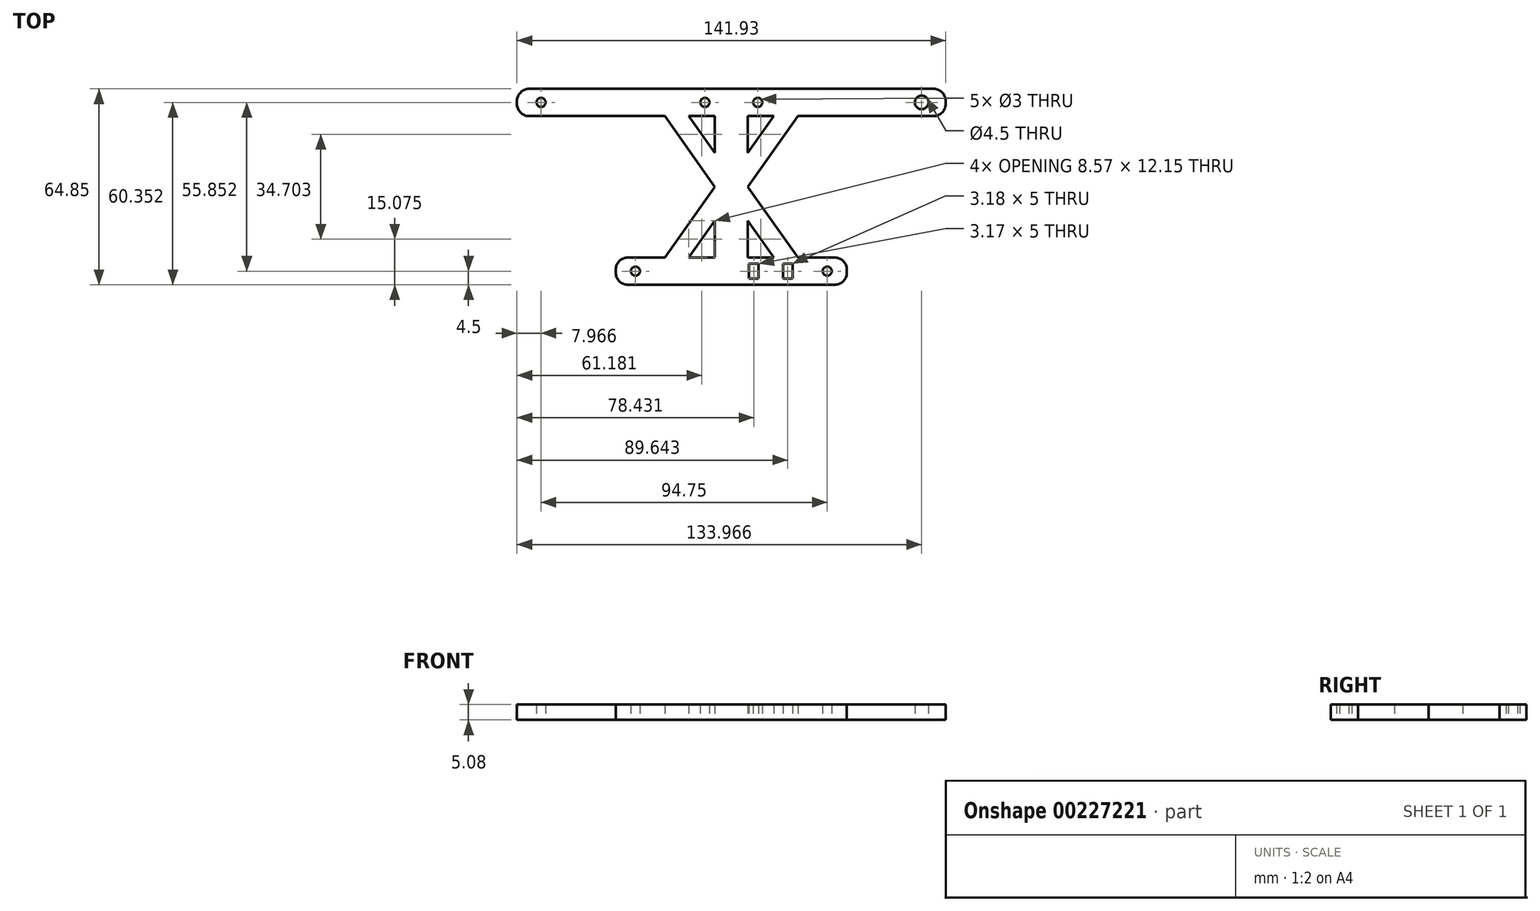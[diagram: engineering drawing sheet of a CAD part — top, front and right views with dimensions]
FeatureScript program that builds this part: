
annotation { "Feature Type Name" : "Feature", "Feature Type Description" : "" }
export const myFeature = defineFeature(function(context is Context, id is Id, definition is map)
    precondition{}
    {
        {
            var Q0;
            Q0=qCreatedBy(makeId("Top.planeOp"),FACE);
            var sketch = newSketch(context, id + "F0", { "sketchPlane" : qUnion([Q0])});
            skCircle(sketch, "E0", {"center": v(-52.08, 55.85) * mm, "radius": 1.5 * mm});
            skCircle(sketch, "E1", {"center": v(-20.83, 0) * mm, "radius": 1.5 * mm});
            skLineSegment(sketch, "E2", {"start": v(-20.83, 0) * mm, "end": v(10.92, 0) * mm});
            skLineSegment(sketch, "E3", {"start": v(-20.83, 0) * mm, "end": v(-52.08, 55.85) * mm});
            skLineSegment(sketch, "E4", {"start": v(-52.08, 55.85) * mm, "end": v(10.92, 55.85) * mm});
            skPoint(sketch, "E5.middle", {"position": v(10.92, 55.85) * mm});
            skPoint(sketch, "E6.middle", {"position": v(10.92, 0) * mm});
            skLineSegment(sketch, "E7", {"start": v(10.92, 0) * mm, "end": v(10.92, 55.85) * mm});
            skPoint(sketch, "E8.middle", {"position": v(10.92, 27.93) * mm});
            skLineSegment(sketch, "E9.MirrorCS", {"start": v(73.92, 55.85) * mm, "end": v(10.92, 55.85) * mm});
            skLineSegment(sketch, "E10.MirrorCS", {"start": v(42.67, 0) * mm, "end": v(73.92, 55.85) * mm});
            skLineSegment(sketch, "E11.MirrorCS", {"start": v(42.67, 0) * mm, "end": v(10.92, 0) * mm});
            skCircle(sketch, "E12.MirrorC", {"center": v(42.67, 0) * mm, "radius": 1.5 * mm});
            skPoint(sketch, "E13.middle", {"position": v(73.92, 55.85) * mm});
            skCircle(sketch, "E14", {"center": v(73.92, 55.85) * mm, "radius": 2.25 * mm});
            skLineSegment(sketch, "E15.bottom", {"start": v(81.88, 60.35) * mm, "end": v(-60.05, 60.35) * mm});
            skLineSegment(sketch, "E15.top", {"start": v(81.88, 51.35) * mm, "end": v(-60.05, 51.35) * mm});
            skLineSegment(sketch, "E15.left", {"start": v(81.88, 60.35) * mm, "end": v(81.88, 51.35) * mm});
            skLineSegment(sketch, "E15.right", {"start": v(-60.05, 60.35) * mm, "end": v(-60.05, 51.35) * mm});
            skLineSegment(sketch, "E16.bottom", {"start": v(49.17, 4.5) * mm, "end": v(-27.34, 4.5) * mm});
            skLineSegment(sketch, "E16.top", {"start": v(49.17, -4.5) * mm, "end": v(-27.34, -4.5) * mm});
            skLineSegment(sketch, "E16.left", {"start": v(49.17, 4.5) * mm, "end": v(49.17, -4.5) * mm});
            skLineSegment(sketch, "E16.right", {"start": v(-27.34, 4.5) * mm, "end": v(-27.34, -4.5) * mm});
            skLineSegment(sketch, "E17", {"start": v(5.42, 51.35) * mm, "end": v(5.42, 4.5) * mm});
            skLineSegment(sketch, "E18.MirrorCS", {"start": v(16.42, 51.35) * mm, "end": v(16.42, 4.5) * mm});
            skLineSegment(sketch, "E19", {"start": v(5.42, 27.93) * mm, "end": v(16.42, 27.93) * mm});
            skLineSegment(sketch, "E20", {"start": v(-11.1, 51.35) * mm, "end": v(5.42, 27.93) * mm});
            skLineSegment(sketch, "E21", {"start": v(-3.15, 51.35) * mm, "end": v(5.42, 39.2) * mm});
            skLineSegment(sketch, "E22.MirrorCS", {"start": v(24.99, 51.35) * mm, "end": v(16.42, 39.2) * mm});
            skLineSegment(sketch, "E23.MirrorCS", {"start": v(32.94, 51.35) * mm, "end": v(16.42, 27.93) * mm});
            skLineSegment(sketch, "E24.MirrorCS", {"start": v(32.94, 4.5) * mm, "end": v(16.42, 27.93) * mm});
            skLineSegment(sketch, "E25.MirrorCS", {"start": v(24.99, 4.5) * mm, "end": v(16.42, 16.65) * mm});
            skLineSegment(sketch, "E26.MirrorCS", {"start": v(-3.15, 4.5) * mm, "end": v(5.42, 16.65) * mm});
            skLineSegment(sketch, "E27.MirrorCS", {"start": v(-11.1, 4.5) * mm, "end": v(5.42, 27.93) * mm});
            skLineSegment(sketch, "E28.bottom", {"start": v(31.18, 2.5) * mm, "end": v(28, 2.5) * mm});
            skLineSegment(sketch, "E28.top", {"start": v(31.18, -2.5) * mm, "end": v(28, -2.5) * mm});
            skLineSegment(sketch, "E28.left", {"start": v(31.18, 2.5) * mm, "end": v(31.18, -2.5) * mm});
            skLineSegment(sketch, "E28.right", {"start": v(28, 2.5) * mm, "end": v(28, -2.5) * mm});
            skPoint(sketch, "E28.middle", {"position": v(29.6, 0) * mm});
            skCircle(sketch, "E29", {"center": v(19.67, 55.85) * mm, "radius": 1.5 * mm});
            skCircle(sketch, "E30.MirrorC", {"center": v(2.17, 55.85) * mm, "radius": 1.5 * mm});
            skLineSegment(sketch, "E31.bottom", {"start": v(19.97, 2.5) * mm, "end": v(16.8, 2.5) * mm});
            skLineSegment(sketch, "E31.top", {"start": v(19.97, -2.5) * mm, "end": v(16.8, -2.5) * mm});
            skLineSegment(sketch, "E31.left", {"start": v(19.97, 2.5) * mm, "end": v(19.97, -2.5) * mm});
            skLineSegment(sketch, "E31.right", {"start": v(16.8, 2.5) * mm, "end": v(16.8, -2.5) * mm});
            skSolve(sketch);
        }
        {
            var Q0;
            {var subQ5=sQuery(id+"F0.wireOp",EDGE,"E0");var subQ7=sQuery(id+"F0.wireOp",EDGE,"E3");var subQ8=makeQuery(id+"F0.imprint","INTERSECT",VERTEX,{"derivedFrom":[subQ5,subQ7]});Q0=makeQuery(id+"F0.imprint","IMPRINT",FACE,{"disambiguationData":[TD([[makeQuery(id+"F0.imprint","IMPRINT",EDGE,{"disambiguationData":[TD([[subQ8,-1.0]])],"derivedFrom":subQ5}),-1.0]])]});}
            var Q1;
            {var subQ1=sQuery(id+"F0.wireOp",EDGE,"E2");var subQ5=sQuery(id+"F0.wireOp",EDGE,"E1");var subQ6=makeQuery(id+"F0.imprint","INTERSECT",VERTEX,{"derivedFrom":[subQ5,subQ1]});Q1=makeQuery(id+"F0.imprint","IMPRINT",FACE,{"disambiguationData":[TD([[makeQuery(id+"F0.imprint","IMPRINT",EDGE,{"disambiguationData":[TD([[subQ6,-1.0]])],"derivedFrom":subQ5}),-1.0]])]});}
            var Q2;
            Q2=makeQuery(id+"F0.imprint","IMPRINT",FACE,{"disambiguationData":[TD([[makeQuery(id+"F0.imprint","IMPRINT",EDGE,{"derivedFrom":sQuery(id+"F0.wireOp",EDGE,"E15.bottom")}),1.0]])]});
            var Q3;
            Q3=makeQuery(id+"F0.imprint","IMPRINT",FACE,{"disambiguationData":[TD([[makeQuery(id+"F0.imprint","IMPRINT",EDGE,{"derivedFrom":sQuery(id+"F0.wireOp",EDGE,"E16.top")}),-1.0]])]});
            var Q4;
            {var subQ1=sQuery(id+"F0.wireOp",EDGE,"E10.MirrorCS");var subQ5=sQuery(id+"F0.wireOp",EDGE,"E16.bottom");var subQ6=makeQuery(id+"F0.imprint","INTERSECT",VERTEX,{"derivedFrom":[subQ1,subQ5]});Q4=makeQuery(id+"F0.imprint","IMPRINT",FACE,{"disambiguationData":[TD([[makeQuery(id+"F0.imprint","IMPRINT",EDGE,{"disambiguationData":[TD([[subQ6,1.0]])],"derivedFrom":subQ1}),1.0]])]});}
            var Q5;
            {var subQ0=sQuery(id+"F0.wireOp",EDGE,"E15.top");var subQ1=sQuery(id+"F0.wireOp",EDGE,"E10.MirrorCS");var subQ2=makeQuery(id+"F0.imprint","INTERSECT",VERTEX,{"derivedFrom":[subQ1,subQ0]});Q5=makeQuery(id+"F0.imprint","IMPRINT",FACE,{"disambiguationData":[TD([[makeQuery(id+"F0.imprint","IMPRINT",EDGE,{"disambiguationData":[TD([[subQ2,-1.0]])],"derivedFrom":subQ1}),1.0]])]});}
            var Q6;
            {var subQ5=sQuery(id+"F0.wireOp",EDGE,"E17");Q6=makeQuery(id+"F0.imprint","IMPRINT",FACE,{"disambiguationData":[TD([[makeQuery(id+"F0.imprint","IMPRINT",EDGE,{"derivedFrom":subQ5}),1.0]])]});}
            var Q7;
            {var subQ5=sQuery(id+"F0.wireOp",EDGE,"E18.MirrorCS");Q7=makeQuery(id+"F0.imprint","IMPRINT",FACE,{"disambiguationData":[TD([[makeQuery(id+"F0.imprint","IMPRINT",EDGE,{"derivedFrom":subQ5}),-1.0]])]});}
            var Q8;
            {var subQ0=sQuery(id+"F0.wireOp",EDGE,"feb966cf-f615-44a7-a13d-1bd144c4b3750.MirrorCS");Q8=makeQuery(id+"F0.imprint","IMPRINT",FACE,{"disambiguationData":[TD([[makeQuery(id+"F0.imprint","IMPRINT",EDGE,{"derivedFrom":subQ0}),-1.0]])]});}
            var Q9;
            {var subQ0=sQuery(id+"F0.wireOp",EDGE,"d3fe900e-5d7e-4329-a638-1e34b492a3660.MirrorCS");Q9=makeQuery(id+"F0.imprint","IMPRINT",FACE,{"disambiguationData":[TD([[makeQuery(id+"F0.imprint","IMPRINT",EDGE,{"derivedFrom":subQ0}),1.0]])]});}
            var Q10;
            {var subQ0=sQuery(id+"F0.wireOp",EDGE,"hfX9tZ72-0kb9-5i1I-bADh-dzFUvOyJdu75");Q10=makeQuery(id+"F0.imprint","IMPRINT",FACE,{"disambiguationData":[TD([[makeQuery(id+"F0.imprint","IMPRINT",EDGE,{"derivedFrom":subQ0}),-1.0]])]});}
            var Q11;
            {var subQ0=sQuery(id+"F0.wireOp",EDGE,"7ac03fb2-961d-4cd1-b936-0828aa2fb5720.MirrorCS");Q11=makeQuery(id+"F0.imprint","IMPRINT",FACE,{"disambiguationData":[TD([[makeQuery(id+"F0.imprint","IMPRINT",EDGE,{"derivedFrom":subQ0}),-1.0]])]});}
            var Q12;
            {var subQ0=sQuery(id+"F0.wireOp",EDGE,"E20");Q12=makeQuery(id+"F0.imprint","IMPRINT",FACE,{"disambiguationData":[TD([[makeQuery(id+"F0.imprint","IMPRINT",EDGE,{"derivedFrom":subQ0}),1.0]])]});}
            var Q13;
            {var subQ0=sQuery(id+"F0.wireOp",EDGE,"E26.MirrorCS");Q13=makeQuery(id+"F0.imprint","IMPRINT",FACE,{"disambiguationData":[TD([[makeQuery(id+"F0.imprint","IMPRINT",EDGE,{"derivedFrom":subQ0}),1.0]])]});}
            var Q14;
            {var subQ0=sQuery(id+"F0.wireOp",EDGE,"E24.MirrorCS");Q14=makeQuery(id+"F0.imprint","IMPRINT",FACE,{"disambiguationData":[TD([[makeQuery(id+"F0.imprint","IMPRINT",EDGE,{"derivedFrom":subQ0}),1.0]])]});}
            var Q15;
            {var subQ0=sQuery(id+"F0.wireOp",EDGE,"E22.MirrorCS");Q15=makeQuery(id+"F0.imprint","IMPRINT",FACE,{"disambiguationData":[TD([[makeQuery(id+"F0.imprint","IMPRINT",EDGE,{"derivedFrom":subQ0}),1.0]])]});}
            extrude(context, id + "F1", {"entities" : qUnion([Q0, Q1, Q2, Q3, Q4, Q5, Q6, Q7, Q8, Q9, Q10, Q11, Q12, Q13, Q14, Q15]), "depth" : 5.08 * mm});
        }
        {
            var Q0;
            Q0=makeQuery(id+"F1.opExtrude","SWEPT_EDGE",EDGE,{"disambiguationData":[OSD([sQuery(id+"F0.wireOp",EDGE,"E15.bottom"),sQuery(id+"F0.wireOp",EDGE,"E15.right")])]});
            var Q1;
            Q1=makeQuery(id+"F1.opExtrude","SWEPT_EDGE",EDGE,{"disambiguationData":[OSD([sQuery(id+"F0.wireOp",EDGE,"E15.top"),sQuery(id+"F0.wireOp",EDGE,"E15.right")])]});
            var Q2;
            Q2=makeQuery(id+"F1.opExtrude","SWEPT_EDGE",EDGE,{"disambiguationData":[OSD([sQuery(id+"F0.wireOp",EDGE,"E15.bottom"),sQuery(id+"F0.wireOp",EDGE,"E15.left")])]});
            var Q3;
            Q3=makeQuery(id+"F1.opExtrude","SWEPT_EDGE",EDGE,{"disambiguationData":[OSD([sQuery(id+"F0.wireOp",EDGE,"E15.top"),sQuery(id+"F0.wireOp",EDGE,"E15.left")])]});
            var Q4;
            Q4=makeQuery(id+"F1.opExtrude","SWEPT_EDGE",EDGE,{"disambiguationData":[OSD([sQuery(id+"F0.wireOp",EDGE,"E16.bottom"),sQuery(id+"F0.wireOp",EDGE,"E16.left")])]});
            var Q5;
            Q5=makeQuery(id+"F1.opExtrude","SWEPT_EDGE",EDGE,{"disambiguationData":[OSD([sQuery(id+"F0.wireOp",EDGE,"E16.top"),sQuery(id+"F0.wireOp",EDGE,"E16.left")])]});
            var Q6;
            Q6=makeQuery(id+"F1.opExtrude","SWEPT_EDGE",EDGE,{"disambiguationData":[OSD([sQuery(id+"F0.wireOp",EDGE,"E16.bottom"),sQuery(id+"F0.wireOp",EDGE,"E16.right")])]});
            var Q7;
            Q7=makeQuery(id+"F1.opExtrude","SWEPT_EDGE",EDGE,{"disambiguationData":[OSD([sQuery(id+"F0.wireOp",EDGE,"E16.top"),sQuery(id+"F0.wireOp",EDGE,"E16.right")])]});
            fillet(context, id + "F2", {"entities" : qUnion([Q0, Q1, Q2, Q3, Q4, Q5, Q6, Q7]), "radius" : 4 * mm, "tangentPropagation" : true, "allowEdgeOverflow" : false});
        }
    });
